# Revit family: Lighting_Pendants_Molto-Luce_Lens-Pendant_
name_source: partatom
category: Lighting Fixtures
revit_build: Autodesk Revit 2018 (Build: 20180423_1000(x64)
units: mm (PartAtom-declared; Revit-internal decimal feet)

## family parameters
Always vertical = No
Cut with Voids When Loaded = No
Light Source = Yes
OmniClass Number = 23.35.45.15
Part Type = Normal
Room Calculation Point = No
Round Connector Dimension = Use Diameter
Shared = No
Work Plane-Based = No

## types (1)
- Default - please load Revit Family Type Catalog
    BIMobject category = Pendants
    BIMobject category code = lighting-pendants
    BIMobject main category = Lighting
    BIMobject main category code = lighting
    Color Filter = 16777215
    Design country = Austria
    Dimming Lamp Color Temperature Shift = <None>
    Edition number = 1
    Emit from Line Length = 1435 mm  [stored 4.70801 ft]
    Geometry 1 = Yes
    Geometry 2 = No
    Geometry 3 = No
    Geometry 4 = No
    IFC Classification = Lamp
    Light Source Symbol Size = 609.6 mm  [stored 2 ft]
    Long = No
    Manufacturer country = Austria
    Manufacturer name = Molto Luce
    Masterformat 2014 Code = 26 50 00
    Masterformat 2014 Description = Lighting
    Material main = Aluminium
    Material secondary = Acrylic
    NBS Reference Code = 49
    NBS Reference Description = Luminaires And Lamps
    OmniClass Code = 23-35 45 15
    OmniClass Description = Lamps
    Placement - (Double) Color temperature - (4000K) Motion detector and dimmability - (Motion detector)  Color of body - (Aluminium anodised) = No
    Placement - (Quad Double) Color temperature - (3000K) Motion detector and dimmability - (No)  Color of body - (Aluminium anodised) = No
    Placement - (Quad Double) Color temperature - (3000K) Motion detector and dimmability - (No)  Color of body - (Aluminium anodised)_1 = No
    Placement - (Quad Double) Color temperature - (4000K) Motion detector and dimmability - (Motion detector)  Color of body - (Aluminium anodised) = No
    Placement - (Quad Short) Color temperature - (4000K) Motion detector and dimmability - (Motion detector)  Color of body - (White) = No
    Placement - (Quad Short) Color temperature - (4000K) Motion detector and dimmability - (No)  Color of body - (White) = No
    Placement - (Single Short) Color temperature - (3000K) Motion detector and dimmability - (Motion detector)  Color of body - (Aluminium anodised) = No
    Placement - (Single Short) Color temperature - (3000K) Motion detector and dimmability - (Motion detector)  Color of body - (Aluminium anodised)_1 = No
    Placement - (Single Short) Color temperature - (3000K) Motion detector and dimmability - (Motion detector)  Color of body - (Aluminium anodised)_2 = Yes
    Placement - (Single) Color temperature - (3000K) Motion detector and dimmability - (No)  Color of body - (Aluminium anodised) = Yes
    Product Guid = caa1e543-230d-427b-a360-9a6dafc1e694
    Product SKU = Lens_Pendant
    Product data url = https://bimobject.com
    Product family = Lighting
    Product group = Pendant Lamp
    Product name = Lens Pendant
    QR code = http://bimobject.com
    Short = Yes
    UNSPSC Code = 3911
    Uniclass 1.4 Code = JY73
    Uniclass 1.4 Description = Luminaires and lamps
    Uniclass 2.0 Code = PR-49
    Uniclass 2.0 Description = Luminaires And Lamps
    Uniclass 2015 Code = Pr_70_70_48
    Uniclass 2015 Name = Luminaires, lighting track and lighting accessories
    Uniformat II Code = D5020
    Uniformat II Description = Lighting & Branch Wiring

note: [stored X ft] marks values corroborated as IEEE doubles in the binary element streams (Revit-internal decimal feet)

## geometry (parser evidence)
native form markers: Blend x2, Sweep x3
no freeform markers — native parametric forms only
